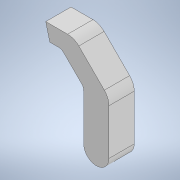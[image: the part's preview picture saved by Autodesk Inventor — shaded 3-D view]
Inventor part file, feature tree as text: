
AUTODESK INVENTOR PART (.ipt)
format: ipt  version: 2021 (Build 250183000, 183)  size: 190,464 bytes
history: native  units: mm
features: extrude x9, sketch x9, chamfer x2, fillet x2
ambient origin geometry x8: Origin, YZ Plane, XZ Plane, XY Plane, X Axis, Y Axis, Z Axis, Center Point
bodies: Body1 (feature_tree)
feature tree (22):
  extrude  "Extrusion2"  Depth=8.0mm
  extrude  "Extrusion3"  Depth=5.0mm TaperAngle=0.0deg
  extrude  "Extrusion4"  Depth=2.5mm
  extrude  "Extrusion6"  Depth=5.0mm TaperAngle=0.0deg
  extrude  "Extrusion7"  Depth=3.0mm
  extrude  "Extrusion8"  Depth=5.0mm
  extrude  "Extrusion10"  Depth=0.8mm
  chamfer  "Chamfer5"  Distance=5.0mm
  chamfer  "Chamfer6"  Distance=4.2mm
  fillet  "Fillet6"  Radius=5.0mm
  fillet  "Fillet7"  Radius=3.0mm
  extrude  "Extrusion14"  Depth=2.0mm TaperAngle=45.0deg
  extrude  "Extrusion15"  Depth=2.0mm TaperAngle=45.0deg
  sketch  "Sketch2"  dims[d11=8.0mm d12=8.0mm]
  sketch  "Sketch3"  dims[d13=25.0mm d14=5.0mm d15=0.0mm]
  sketch  "Sketch4"  dims[d16=2.5mm d17=2.5mm]
  sketch  "Sketch6"  dims[d18=20.0mm d19=5.0mm d20=0.0mm]
  sketch  "Sketch7"  dims[d21=3.0mm d22=0.0mm d30=7.0mm]
  sketch  "Sketch8"  dims[d31=5.0mm d32=0.0mm d33=1.0mm]
  sketch  "Sketch10"  dims[d34=6.0mm d35=0.8mm]
  sketch  "Sketch14"  dims[d36=0.8mm d37=5.0mm d38=0.0mm]
  sketch  "Sketch15"  dims[d39=16.0mm d40=4.2mm d41=5.0mm d42=0.0mm d55=3.0mm d56=0.0mm d65=7.0mm d66=2.0mm d67=45.0deg d68=11.0mm d69=2.0mm d70=45.0deg d75=5.0mm d79=2.0mm d80=3.0mm d81=0.0mm d82=1.3mm d83=20.0mm d84=0.0mm]
